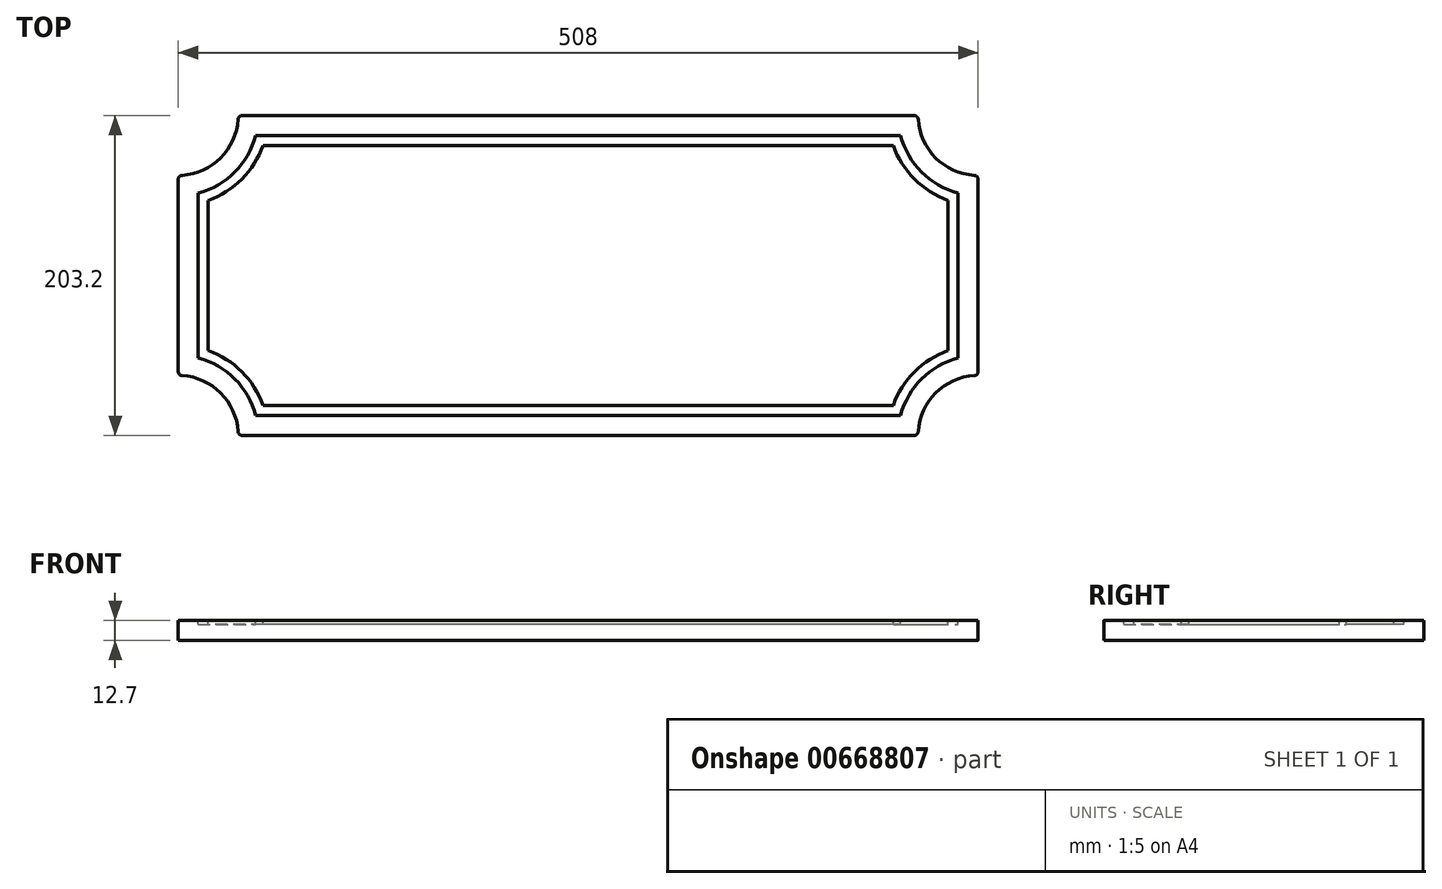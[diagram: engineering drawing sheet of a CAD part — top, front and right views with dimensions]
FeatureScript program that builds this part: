
annotation { "Feature Type Name" : "Feature", "Feature Type Description" : "" }
export const myFeature = defineFeature(function(context is Context, id is Id, definition is map)
    precondition{}
    {
        {
            var Q0;
            Q0=qCreatedBy(makeId("Top.planeOp"),FACE);
            var sketch = newSketch(context, id + "F0", { "sketchPlane" : qUnion([Q0])});
            skLineSegment(sketch, "E0.bottom", {"start": v(215.9, -101.6) * mm, "end": v(-215.9, -101.6) * mm});
            skLineSegment(sketch, "E0.top", {"start": v(215.9, 101.6) * mm, "end": v(-215.9, 101.6) * mm});
            skLineSegment(sketch, "E0.left", {"start": v(254, -63.5) * mm, "end": v(254, 63.5) * mm});
            skLineSegment(sketch, "E0.right", {"start": v(-254, -63.5) * mm, "end": v(-254, 63.5) * mm});
            skPoint(sketch, "E0.middle", {"position": v(0, 0) * mm});
            skArc(sketch, "E1", {"start": v(215.9, 101.6) * mm, "mid": v(227.06, 74.66) * mm, "end": v(254, 63.5) * mm});
            skLineSegment(sketch, "E2", {"start": v(0, 0) * mm, "end": v(0, 142.87) * mm, "construction": true});
            skArc(sketch, "E3.MirrorCS", {"start": v(-215.9, 101.6) * mm, "mid": v(-227.06, 74.66) * mm, "end": v(-254, 63.5) * mm});
            skLineSegment(sketch, "E4", {"start": v(0, 0) * mm, "end": v(334.72, 0) * mm, "construction": true});
            skArc(sketch, "E5.MirrorCS", {"start": v(215.9, -101.6) * mm, "mid": v(227.06, -74.66) * mm, "end": v(254, -63.5) * mm});
            skArc(sketch, "E6.MirrorCS", {"start": v(-215.9, -101.6) * mm, "mid": v(-227.06, -74.66) * mm, "end": v(-254, -63.5) * mm});
            skSolve(sketch);
        }
        {
            var Q0;
            Q0=makeQuery(id+"F0.imprint","IMPRINT",FACE,{"disambiguationData":[TD([[makeQuery(id+"F0.imprint","IMPRINT",EDGE,{"derivedFrom":sQuery(id+"F0.wireOp",EDGE,"E0.bottom")}),-1.0]])]});
            extrude(context, id + "F1", {"entities" : qUnion([Q0]), "oppositeDirection" : true, "depth" : 12.7 * mm, "offsetDistance" : 25.4 * mm});
        }
        {
            var Q0;
            Q0=makeQuery(id+"F1.opExtrude","CAP_FACE",FACE,{"disambiguationData":[OSD([sQuery(id+"F0.wireOp",EDGE,"E0.bottom"),sQuery(id+"F0.wireOp",EDGE,"E0.top"),sQuery(id+"F0.wireOp",EDGE,"E0.left"),sQuery(id+"F0.wireOp",EDGE,"E0.right"),sQuery(id+"F0.wireOp",EDGE,"E1"),sQuery(id+"F0.wireOp",EDGE,"E3.MirrorCS"),sQuery(id+"F0.wireOp",EDGE,"E5.MirrorCS"),sQuery(id+"F0.wireOp",EDGE,"E6.MirrorCS")])],"isStart":true});
            var sketch = newSketch(context, id + "F2", { "sketchPlane" : qUnion([Q0])});
            skArc(sketch, "E7.0", {"start": v(204.81, 88.9) * mm, "mid": v(218.08, 65.68) * mm, "end": v(241.3, 52.41) * mm});
            skLineSegment(sketch, "E7.1", {"start": v(241.3, -52.41) * mm, "end": v(241.3, 52.41) * mm});
            skLineSegment(sketch, "E7.2", {"start": v(204.81, 88.9) * mm, "end": v(-204.81, 88.9) * mm});
            skArc(sketch, "E7.3", {"start": v(204.81, -88.9) * mm, "mid": v(218.08, -65.68) * mm, "end": v(241.3, -52.41) * mm});
            skArc(sketch, "E7.4", {"start": v(-204.81, 88.9) * mm, "mid": v(-218.08, 65.68) * mm, "end": v(-241.3, 52.41) * mm});
            skLineSegment(sketch, "E7.5", {"start": v(-241.3, -52.41) * mm, "end": v(-241.3, 52.41) * mm});
            skArc(sketch, "E7.6", {"start": v(-204.81, -88.9) * mm, "mid": v(-218.08, -65.68) * mm, "end": v(-241.3, -52.41) * mm});
            skLineSegment(sketch, "E7.7", {"start": v(204.81, -88.9) * mm, "end": v(-204.81, -88.9) * mm});
            skArc(sketch, "E8.0", {"start": v(200.12, 82.55) * mm, "mid": v(213.59, 61.19) * mm, "end": v(234.95, 47.72) * mm});
            skLineSegment(sketch, "E8.1", {"start": v(234.95, -47.72) * mm, "end": v(234.95, 47.72) * mm});
            skLineSegment(sketch, "E8.2", {"start": v(200.12, 82.55) * mm, "end": v(-200.12, 82.55) * mm});
            skArc(sketch, "E8.3", {"start": v(200.12, -82.55) * mm, "mid": v(213.59, -61.19) * mm, "end": v(234.95, -47.72) * mm});
            skArc(sketch, "E8.4", {"start": v(-200.12, 82.55) * mm, "mid": v(-213.59, 61.19) * mm, "end": v(-234.95, 47.72) * mm});
            skLineSegment(sketch, "E8.5", {"start": v(-234.95, -47.72) * mm, "end": v(-234.95, 47.72) * mm});
            skArc(sketch, "E8.6", {"start": v(-200.12, -82.55) * mm, "mid": v(-213.59, -61.19) * mm, "end": v(-234.95, -47.72) * mm});
            skLineSegment(sketch, "E8.7", {"start": v(200.12, -82.55) * mm, "end": v(-200.12, -82.55) * mm});
            skLineSegment(sketch, "E9.0", {"start": v(215.9, 101.6) * mm, "end": v(-215.9, 101.6) * mm});
            skArc(sketch, "E10.0", {"start": v(-215.9, 101.6) * mm, "mid": v(-227.06, 74.66) * mm, "end": v(-254, 63.5) * mm});
            skLineSegment(sketch, "E11.0", {"start": v(-254, -63.5) * mm, "end": v(-254, 63.5) * mm});
            skArc(sketch, "E12.0", {"start": v(-215.9, -101.6) * mm, "mid": v(-227.06, -74.66) * mm, "end": v(-254, -63.5) * mm});
            skLineSegment(sketch, "E13.0", {"start": v(215.9, -101.6) * mm, "end": v(-215.9, -101.6) * mm});
            skArc(sketch, "E14.0", {"start": v(215.9, -101.6) * mm, "mid": v(227.06, -74.66) * mm, "end": v(254, -63.5) * mm});
            skLineSegment(sketch, "E15.0", {"start": v(254, -63.5) * mm, "end": v(254, 63.5) * mm});
            skArc(sketch, "E16.0", {"start": v(215.9, 101.6) * mm, "mid": v(227.06, 74.66) * mm, "end": v(254, 63.5) * mm});
            skSolve(sketch);
        }
        {
            var Q0;
            Q0=makeQuery(id+"F2.imprint","IMPRINT",FACE,{"disambiguationData":[TD([[makeQuery(id+"F2.imprint","IMPRINT",EDGE,{"derivedFrom":sQuery(id+"F2.wireOp",EDGE,"E7.0")}),-1.0]])]});
            extrude(context, id + "F3", {"entities" : qUnion([Q0]), "operationType" : NewBodyOperationType.REMOVE, "oppositeDirection" : true, "depth" : 2.54 * mm, "offsetDistance" : 25.4 * mm});
        }
        {
            var Q0;
            Q0=makeQuery(id+"F1.opExtrude","SWEPT_EDGE",EDGE,{"disambiguationData":[OSD([sQuery(id+"F0.wireOp",EDGE,"E0.right"),sQuery(id+"F0.wireOp",EDGE,"E3.MirrorCS")])]});
            var Q1;
            Q1=makeQuery(id+"F1.opExtrude","SWEPT_EDGE",EDGE,{"disambiguationData":[OSD([sQuery(id+"F0.wireOp",EDGE,"E0.top"),sQuery(id+"F0.wireOp",EDGE,"E3.MirrorCS")])]});
            var Q2;
            Q2=makeQuery(id+"F1.opExtrude","SWEPT_EDGE",EDGE,{"disambiguationData":[OSD([sQuery(id+"F0.wireOp",EDGE,"E0.left"),sQuery(id+"F0.wireOp",EDGE,"E1")])]});
            var Q3;
            Q3=makeQuery(id+"F1.opExtrude","SWEPT_EDGE",EDGE,{"disambiguationData":[OSD([sQuery(id+"F0.wireOp",EDGE,"E0.top"),sQuery(id+"F0.wireOp",EDGE,"E1")])]});
            var Q4;
            Q4=makeQuery(id+"F1.opExtrude","SWEPT_EDGE",EDGE,{"disambiguationData":[OSD([sQuery(id+"F0.wireOp",EDGE,"E0.left"),sQuery(id+"F0.wireOp",EDGE,"E5.MirrorCS")])]});
            var Q5;
            Q5=makeQuery(id+"F1.opExtrude","SWEPT_EDGE",EDGE,{"disambiguationData":[OSD([sQuery(id+"F0.wireOp",EDGE,"E0.bottom"),sQuery(id+"F0.wireOp",EDGE,"E5.MirrorCS")])]});
            var Q6;
            Q6=makeQuery(id+"F1.opExtrude","SWEPT_EDGE",EDGE,{"disambiguationData":[OSD([sQuery(id+"F0.wireOp",EDGE,"E0.bottom"),sQuery(id+"F0.wireOp",EDGE,"E6.MirrorCS")])]});
            var Q7;
            Q7=makeQuery(id+"F1.opExtrude","SWEPT_EDGE",EDGE,{"disambiguationData":[OSD([sQuery(id+"F0.wireOp",EDGE,"E0.right"),sQuery(id+"F0.wireOp",EDGE,"E6.MirrorCS")])]});
            fillet(context, id + "F4", {"entities" : qUnion([Q0, Q1, Q2, Q3, Q4, Q5, Q6, Q7]), "radius" : 2.54 * mm, "tangentPropagation" : true, "allowEdgeOverflow" : false});
        }
    });
